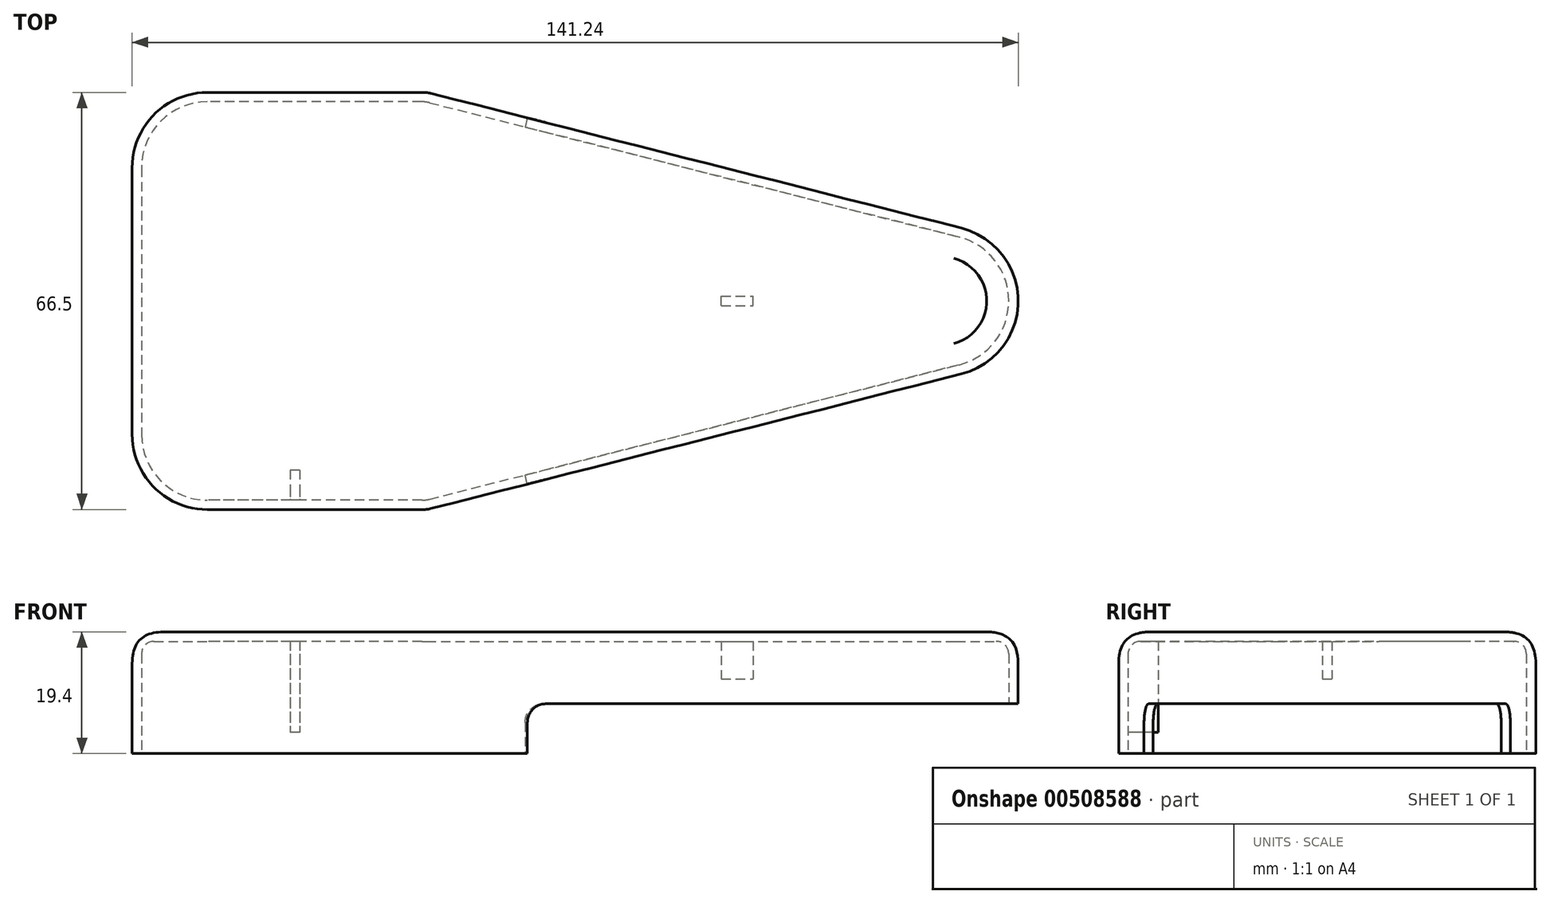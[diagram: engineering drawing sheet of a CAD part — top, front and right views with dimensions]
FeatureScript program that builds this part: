
annotation { "Feature Type Name" : "Feature", "Feature Type Description" : "" }
export const myFeature = defineFeature(function(context is Context, id is Id, definition is map)
    precondition{}
    {
        {
            var Q0;
            Q0=qCreatedBy(makeId("Top.planeOp"),FACE);
            var sketch = newSketch(context, id + "F0", { "sketchPlane" : qUnion([Q0])});
            skLineSegment(sketch, "E0.bottom", {"start": v(-70.61, 33.25) * mm, "end": v(70.61, 33.25) * mm, "construction": true});
            skLineSegment(sketch, "E0.top", {"start": v(-70.61, -33.25) * mm, "end": v(70.61, -33.25) * mm, "construction": true});
            skLineSegment(sketch, "E0.left", {"start": v(-70.61, 33.25) * mm, "end": v(-70.61, -33.25) * mm, "construction": true});
            skLineSegment(sketch, "E0.right", {"start": v(70.61, 33.25) * mm, "end": v(70.61, -33.25) * mm, "construction": true});
            skPoint(sketch, "E0.middle", {"position": v(0, 0) * mm});
            skLineSegment(sketch, "E1", {"start": v(-23.61, 33.25) * mm, "end": v(-23.62, -33.25) * mm, "construction": true});
            skArc(sketch, "E2", {"start": v(-58.62, 33.25) * mm, "mid": v(-67.1, 29.74) * mm, "end": v(-70.62, 21.25) * mm});
            skArc(sketch, "E3", {"start": v(-70.62, -21.25) * mm, "mid": v(-67.1, -29.74) * mm, "end": v(-58.62, -33.25) * mm});
            skArc(sketch, "E4", {"start": v(61.57, -11.63) * mm, "mid": v(70.61, 0) * mm, "end": v(61.57, 11.63) * mm});
            skLineSegment(sketch, "E5", {"start": v(-23.62, 33.25) * mm, "end": v(61.57, 11.63) * mm});
            skLineSegment(sketch, "E6", {"start": v(-23.62, -33.25) * mm, "end": v(61.57, -11.63) * mm});
            skLineSegment(sketch, "E7", {"start": v(-23.61, 33.25) * mm, "end": v(-58.62, 33.25) * mm});
            skLineSegment(sketch, "E8", {"start": v(-70.62, 21.25) * mm, "end": v(-70.62, -21.25) * mm});
            skLineSegment(sketch, "E9", {"start": v(-23.62, -33.25) * mm, "end": v(-58.62, -33.25) * mm});
            skSolve(sketch);
        }
        {
            var Q0;
            Q0=makeQuery(id+"F0.imprint","IMPRINT",FACE,{"disambiguationData":[TD([[makeQuery(id+"F0.imprint","IMPRINT",EDGE,{"derivedFrom":sQuery(id+"F0.wireOp",EDGE,"E2")}),1.0]])]});
            extrude(context, id + "F1", {"entities" : qUnion([Q0]), "depth" : 19.4 * mm, "offsetDistance" : 25 * mm});
        }
        {
            var Q0;
            Q0=makeQuery(id+"F1.opExtrude","CAP_FACE",FACE,{"disambiguationData":[OSD([sQuery(id+"F0.wireOp",EDGE,"E2"),sQuery(id+"F0.wireOp",EDGE,"E3"),sQuery(id+"F0.wireOp",EDGE,"E4"),sQuery(id+"F0.wireOp",EDGE,"E5"),sQuery(id+"F0.wireOp",EDGE,"E6"),sQuery(id+"F0.wireOp",EDGE,"E7"),sQuery(id+"F0.wireOp",EDGE,"E8"),sQuery(id+"F0.wireOp",EDGE,"E9")])],"isStart":true});
            shell(context, id + "F2", {"entities" : qUnion([Q0]), "thickness" : 1.5 * mm});
        }
        {
            var Q0;
            Q0=makeQuery(id+"F1.opExtrude","SWEPT_FACE",FACE,{"disambiguationData":[OSD([sQuery(id+"F0.wireOp",EDGE,"E9")])]});
            var sketch = newSketch(context, id + "F3", { "sketchPlane" : qUnion([Q0])});
            skLineSegment(sketch, "E10.0", {"start": v(-23.62, 19.4) * mm, "end": v(-58.62, 19.4) * mm, "construction": true});
            skLineSegment(sketch, "E11.0", {"start": v(-23.62, 0) * mm, "end": v(-58.62, 0) * mm, "construction": true});
            skLineSegment(sketch, "E12", {"start": v(-7.62, 7.94) * mm, "end": v(89.39, 7.94) * mm});
            skLineSegment(sketch, "E13", {"start": v(-7.62, 7.94) * mm, "end": v(-7.62, -17.76) * mm});
            skLineSegment(sketch, "E14", {"start": v(-7.62, -17.76) * mm, "end": v(89.39, -17.76) * mm});
            skLineSegment(sketch, "E15", {"start": v(89.39, -17.76) * mm, "end": v(89.39, 7.94) * mm});
            skSolve(sketch);
        }
        {
            var Q0;
            Q0=makeQuery(id+"F3.imprint","IMPRINT",FACE,{"disambiguationData":[TD([[makeQuery(id+"F3.imprint","IMPRINT",EDGE,{"derivedFrom":sQuery(id+"F3.wireOp",EDGE,"E12")}),-1.0]])]});
            extrude(context, id + "F4", {"entities" : qUnion([Q0]), "operationType" : NewBodyOperationType.REMOVE, "endBound" : BoundingType.THROUGH_ALL, "oppositeDirection" : true, "depth" : 117.7 * mm, "offsetDistance" : 25 * mm});
        }
        {
            var Q0;
            Q0=makeQuery(id+"F1.opExtrude","CAP_FACE",FACE,{"disambiguationData":[OSD([sQuery(id+"F0.wireOp",EDGE,"E2"),sQuery(id+"F0.wireOp",EDGE,"E3"),sQuery(id+"F0.wireOp",EDGE,"E4"),sQuery(id+"F0.wireOp",EDGE,"E5"),sQuery(id+"F0.wireOp",EDGE,"E6"),sQuery(id+"F0.wireOp",EDGE,"E7"),sQuery(id+"F0.wireOp",EDGE,"E8"),sQuery(id+"F0.wireOp",EDGE,"E9")])],"isStart":true});
            var sketch = newSketch(context, id + "F5", { "sketchPlane" : qUnion([Q0])});
            skLineSegment(sketch, "E16.0", {"start": v(61.2, 10.18) * mm, "end": v(-7.61, 27.64) * mm, "construction": true});
            skLineSegment(sketch, "E17.0", {"start": v(61.2, -10.18) * mm, "end": v(-7.62, -27.64) * mm, "construction": true});
            skLineSegment(sketch, "E18.0", {"start": v(61.57, 11.63) * mm, "end": v(-7.61, 29.19) * mm, "construction": true});
            skLineSegment(sketch, "E19.0", {"start": v(61.57, -11.63) * mm, "end": v(-7.61, -29.19) * mm, "construction": true});
            skLineSegment(sketch, "E20", {"start": v(-7.16, 31) * mm, "end": v(-8.52, 25.64) * mm});
            skLineSegment(sketch, "E21", {"start": v(-7.16, 31) * mm, "end": v(-6.28, 30.77) * mm});
            skLineSegment(sketch, "E22", {"start": v(-6.28, 30.77) * mm, "end": v(-7.64, 25.41) * mm});
            skLineSegment(sketch, "E23", {"start": v(-8.52, 25.64) * mm, "end": v(-7.64, 25.41) * mm});
            skLineSegment(sketch, "E24.MirrorCS", {"start": v(-6.28, -30.77) * mm, "end": v(-7.64, -25.41) * mm});
            skLineSegment(sketch, "E25.MirrorCS", {"start": v(-7.16, -31) * mm, "end": v(-6.28, -30.77) * mm});
            skLineSegment(sketch, "E26.MirrorCS", {"start": v(-7.16, -31) * mm, "end": v(-8.52, -25.64) * mm});
            skLineSegment(sketch, "E27.MirrorCS", {"start": v(-8.52, -25.64) * mm, "end": v(-7.64, -25.41) * mm});
            skSolve(sketch);
        }
        {
            var Q0;
            {var subQ1=sQuery(id+"F0.wireOp",EDGE,"E5");var subQ2=makeQuery(id+"F4.boolean.opBoolean","INTERSECT",EDGE,{"disambiguationData":[OD(0.0)],"derivedFrom":[makeQuery(id+"F1.opExtrude","CAP_FACE",FACE,{"disambiguationData":[OSD([sQuery(id+"F0.wireOp",EDGE,"E2"),sQuery(id+"F0.wireOp",EDGE,"E3"),sQuery(id+"F0.wireOp",EDGE,"E4"),subQ1,sQuery(id+"F0.wireOp",EDGE,"E6"),sQuery(id+"F0.wireOp",EDGE,"E7"),sQuery(id+"F0.wireOp",EDGE,"E8"),sQuery(id+"F0.wireOp",EDGE,"E9")])],"isStart":true}),makeQuery(id+"F4.opExtrude","SWEPT_FACE",FACE,{"disambiguationData":[OSD([sQuery(id+"F3.wireOp",EDGE,"E13")])]})]});Q0=makeQuery(id+"F5.imprint","IMPRINT",FACE,{"disambiguationData":[TD([[makeQuery(id+"F5.imprint","IMPRINT",EDGE,{"derivedFrom":subQ2}),1.0]])]});}
            var Q1;
            {var subQ1=sQuery(id+"F0.wireOp",EDGE,"E6");var subQ2=makeQuery(id+"F4.boolean.opBoolean","INTERSECT",EDGE,{"disambiguationData":[OD(1.0)],"derivedFrom":[makeQuery(id+"F1.opExtrude","CAP_FACE",FACE,{"disambiguationData":[OSD([sQuery(id+"F0.wireOp",EDGE,"E2"),sQuery(id+"F0.wireOp",EDGE,"E3"),sQuery(id+"F0.wireOp",EDGE,"E4"),sQuery(id+"F0.wireOp",EDGE,"E5"),subQ1,sQuery(id+"F0.wireOp",EDGE,"E7"),sQuery(id+"F0.wireOp",EDGE,"E8"),sQuery(id+"F0.wireOp",EDGE,"E9")])],"isStart":true}),makeQuery(id+"F4.opExtrude","SWEPT_FACE",FACE,{"disambiguationData":[OSD([sQuery(id+"F3.wireOp",EDGE,"E13")])]})]});Q1=makeQuery(id+"F5.imprint","IMPRINT",FACE,{"disambiguationData":[TD([[makeQuery(id+"F5.imprint","IMPRINT",EDGE,{"derivedFrom":subQ2}),1.0]])]});}
            var Q2;
            Q2=makeQuery(id+"F4.boolean.opBoolean","COPY",FACE,{"derivedFrom":makeQuery(id+"F4.opExtrude","SWEPT_FACE",FACE,{"disambiguationData":[OSD([sQuery(id+"F3.wireOp",EDGE,"E12")])]})});
            extrude(context, id + "F6", {"entities" : qUnion([Q0, Q1]), "operationType" : NewBodyOperationType.REMOVE, "endBound" : BoundingType.UP_TO_SURFACE, "oppositeDirection" : true, "depth" : 25 * mm, "endBoundEntityFace" : qUnion([Q2]), "offsetDistance" : 25 * mm});
        }
        {
            var Q0;
            Q0=makeQuery(id+"F2.opShell","OFFSET_FACE",FACE,{"disambiguationData":[OSD([sQuery(id+"F0.wireOp",EDGE,"E2"),sQuery(id+"F0.wireOp",EDGE,"E3"),sQuery(id+"F0.wireOp",EDGE,"E4"),sQuery(id+"F0.wireOp",EDGE,"E5"),sQuery(id+"F0.wireOp",EDGE,"E6"),sQuery(id+"F0.wireOp",EDGE,"E7"),sQuery(id+"F0.wireOp",EDGE,"E8"),sQuery(id+"F0.wireOp",EDGE,"E9")])]});
            cPlane(context, id + "F7", {"entities" : qUnion([Q0]), "cplaneType" : CPlaneType.OFFSET, "offset" : 14.5 * mm, "width" : 150 * mm, "height" : 150 * mm});
        }
        {
            var Q0;
            Q0=qCreatedBy(id+"F7.planeOp",FACE);
            var sketch = newSketch(context, id + "F8", { "sketchPlane" : qUnion([Q0])});
            skLineSegment(sketch, "E28.0", {"start": v(-70.62, -21.25) * mm, "end": v(-70.62, 21.25) * mm, "construction": true});
            skLineSegment(sketch, "E29.0", {"start": v(-23.8, -31.75) * mm, "end": v(-58.62, -31.75) * mm, "construction": true});
            skLineSegment(sketch, "E30", {"start": v(-43.92, 31.75) * mm, "end": v(-43.91, -31.75) * mm, "construction": true});
            skLineSegment(sketch, "E31", {"start": v(-57.03, 26.95) * mm, "end": v(-36.15, 26.95) * mm, "construction": true});
            skLineSegment(sketch, "E32.0", {"start": v(-23.62, 33.25) * mm, "end": v(-58.62, 33.25) * mm, "construction": true});
            skPoint(sketch, "E33.orphan", {"position": v(-58.62, 31.75) * mm});
            skPoint(sketch, "E34.0.start.orphan", {"position": v(-23.8, 31.75) * mm});
            skLineSegment(sketch, "E35.0", {"start": v(-23.8, 31.75) * mm, "end": v(-58.62, 31.75) * mm, "construction": true});
            skPoint(sketch, "E36", {"position": v(-43.92, 26.95) * mm});
            skLineSegment(sketch, "E37.bottom", {"start": v(-43.92, 26.95) * mm, "end": v(-45.42, 26.95) * mm});
            skLineSegment(sketch, "E37.top", {"start": v(-43.92, 31.75) * mm, "end": v(-45.42, 31.75) * mm});
            skLineSegment(sketch, "E37.left", {"start": v(-43.92, 26.95) * mm, "end": v(-43.92, 31.75) * mm});
            skLineSegment(sketch, "E37.right", {"start": v(-45.42, 26.95) * mm, "end": v(-45.42, 31.75) * mm});
            skSolve(sketch);
        }
        {
            var Q0;
            {var subQ0=sQuery(id+"F0.wireOp",EDGE,"E9");Q0=makeQuery(id+"F2.opShell","OFFSET_EDGE",EDGE,{"disambiguationData":[OSD([subQ0]),TDD([makeQuery(id+"F1.opExtrude","CAP_EDGE",EDGE,{"disambiguationData":[OSD([subQ0])],"isStart":false})])]});}
            var Q1;
            {var subQ0=sQuery(id+"F0.wireOp",EDGE,"E6");Q1=makeQuery(id+"F2.opShell","OFFSET_EDGE",EDGE,{"disambiguationData":[OSD([subQ0]),TDD([makeQuery(id+"F1.opExtrude","CAP_EDGE",EDGE,{"disambiguationData":[OSD([subQ0])],"isStart":false})])]});}
            fillet(context, id + "F9", {"entities" : qUnion([Q0, Q1]), "radius" : 2 * mm, "tangentPropagation" : true, "allowEdgeOverflow" : false});
        }
        {
            var Q0;
            Q0=makeQuery(id+"F8.imprint","IMPRINT",FACE,{"disambiguationData":[TD([[makeQuery(id+"F8.imprint","IMPRINT",EDGE,{"derivedFrom":sQuery(id+"F8.wireOp",EDGE,"E37.bottom")}),-1.0]])]});
            extrude(context, id + "F10", {"entities" : qUnion([Q0]), "operationType" : NewBodyOperationType.ADD, "endBound" : BoundingType.UP_TO_NEXT, "oppositeDirection" : true, "depth" : 25 * mm, "offsetDistance" : 25 * mm});
        }
        {
            var Q0;
            Q0=makeQuery(id+"F2.opShell","OFFSET_FACE",FACE,{"disambiguationData":[OSD([sQuery(id+"F0.wireOp",EDGE,"E2"),sQuery(id+"F0.wireOp",EDGE,"E3"),sQuery(id+"F0.wireOp",EDGE,"E4"),sQuery(id+"F0.wireOp",EDGE,"E5"),sQuery(id+"F0.wireOp",EDGE,"E6"),sQuery(id+"F0.wireOp",EDGE,"E7"),sQuery(id+"F0.wireOp",EDGE,"E8"),sQuery(id+"F0.wireOp",EDGE,"E9")])]});
            var sketch = newSketch(context, id + "F11", { "sketchPlane" : qUnion([Q0])});
            skLineSegment(sketch, "E38.0", {"start": v(-70.62, -21.25) * mm, "end": v(-70.62, 21.25) * mm, "construction": true});
            skLineSegment(sketch, "E39", {"start": v(-24.76, 0) * mm, "end": v(55.29, 0) * mm, "construction": true});
            skLineSegment(sketch, "E40", {"start": v(28.38, 14.2) * mm, "end": v(28.38, -12.8) * mm, "construction": true});
            skLineSegment(sketch, "E41", {"start": v(23.28, 11.59) * mm, "end": v(23.28, -11.77) * mm, "construction": true});
            skLineSegment(sketch, "E42.bottom", {"start": v(23.28, 0.75) * mm, "end": v(28.38, 0.75) * mm});
            skLineSegment(sketch, "E42.top", {"start": v(23.28, -0.75) * mm, "end": v(28.38, -0.75) * mm});
            skLineSegment(sketch, "E42.left", {"start": v(23.28, 0.75) * mm, "end": v(23.28, -0.75) * mm});
            skLineSegment(sketch, "E42.right", {"start": v(28.38, 0.75) * mm, "end": v(28.38, -0.75) * mm});
            skPoint(sketch, "E42.middle", {"position": v(25.83, 0) * mm});
            skSolve(sketch);
        }
        {
            var Q0;
            Q0=makeQuery(id+"F11.imprint","IMPRINT",FACE,{"disambiguationData":[TD([[makeQuery(id+"F11.imprint","IMPRINT",EDGE,{"derivedFrom":sQuery(id+"F11.wireOp",EDGE,"E42.bottom")}),1.0]])]});
            cPlane(context, id + "F12", {"entities" : qUnion([Q0]), "cplaneType" : CPlaneType.OFFSET, "offset" : 6 * mm, "width" : 150 * mm, "height" : 150 * mm});
        }
        {
            var Q0;
            Q0=qCreatedBy(id+"F12.planeOp",FACE);
            var sketch = newSketch(context, id + "F13", { "sketchPlane" : qUnion([Q0])});
            skLineSegment(sketch, "E43.0", {"start": v(23.28, -0.75) * mm, "end": v(28.38, -0.75) * mm});
            skLineSegment(sketch, "E44.0", {"start": v(23.28, 0.75) * mm, "end": v(28.38, 0.75) * mm});
            skLineSegment(sketch, "E45.0", {"start": v(28.38, 0.75) * mm, "end": v(28.38, -0.75) * mm});
            skLineSegment(sketch, "E46.0", {"start": v(23.28, 0.75) * mm, "end": v(23.28, -0.75) * mm});
            skSolve(sketch);
        }
        {
            var Q0;
            Q0=makeQuery(id+"F13.imprint","IMPRINT",FACE,{"disambiguationData":[TD([[makeQuery(id+"F13.imprint","IMPRINT",EDGE,{"derivedFrom":sQuery(id+"F13.wireOp",EDGE,"E43.0")}),1.0]])]});
            extrude(context, id + "F14", {"entities" : qUnion([Q0]), "operationType" : NewBodyOperationType.ADD, "endBound" : BoundingType.UP_TO_NEXT, "oppositeDirection" : true, "depth" : 25 * mm, "offsetDistance" : 25 * mm});
        }
        {
            var Q0;
            Q0=makeQuery(id+"F1.opExtrude","SWEPT_EDGE",EDGE,{"disambiguationData":[OSD([sQuery(id+"F0.wireOp",EDGE,"E6"),sQuery(id+"F0.wireOp",EDGE,"E9")])]});
            var Q1;
            Q1=makeQuery(id+"F1.opExtrude","SWEPT_EDGE",EDGE,{"disambiguationData":[OSD([sQuery(id+"F0.wireOp",EDGE,"E5"),sQuery(id+"F0.wireOp",EDGE,"E7")])]});
            fillet(context, id + "F15", {"entities" : qUnion([Q0, Q1]), "radius" : 5 * mm, "tangentPropagation" : true, "rho" : 0.5, "crossSection" : FilletCrossSection.CONIC, "allowEdgeOverflow" : false});
        }
        {
            var Q0;
            Q0=makeQuery(id+"F1.opExtrude","CAP_FACE",FACE,{"disambiguationData":[OSD([sQuery(id+"F0.wireOp",EDGE,"E2"),sQuery(id+"F0.wireOp",EDGE,"E3"),sQuery(id+"F0.wireOp",EDGE,"E4"),sQuery(id+"F0.wireOp",EDGE,"E5"),sQuery(id+"F0.wireOp",EDGE,"E6"),sQuery(id+"F0.wireOp",EDGE,"E7"),sQuery(id+"F0.wireOp",EDGE,"E8"),sQuery(id+"F0.wireOp",EDGE,"E9")])],"isStart":false});
            fillet(context, id + "F16", {"entities" : qUnion([Q0]), "radius" : 5 * mm, "tangentPropagation" : true, "rho" : 0.5, "crossSection" : FilletCrossSection.CONIC, "allowEdgeOverflow" : false});
        }
        {
            var Q0;
            Q0=makeQuery(id+"F6.boolean.opBoolean","COPY",EDGE,{"derivedFrom":makeQuery(id+"F6.opExtrude","CAP_EDGE",EDGE,{"disambiguationData":[OSD([sQuery(id+"F5.wireOp",EDGE,"E20")])],"isStart":true})});
            var Q1;
            Q1=makeQuery(id+"F6.boolean.opBoolean","COPY",EDGE,{"derivedFrom":makeQuery(id+"F6.opExtrude","CAP_EDGE",EDGE,{"disambiguationData":[OSD([sQuery(id+"F5.wireOp",EDGE,"E20")])],"isStart":false})});
            var Q2;
            Q2=makeQuery(id+"F6.boolean.opBoolean","COPY",EDGE,{"derivedFrom":makeQuery(id+"F6.opExtrude","CAP_EDGE",EDGE,{"disambiguationData":[OSD([sQuery(id+"F5.wireOp",EDGE,"E26.MirrorCS")])],"isStart":true})});
            var Q3;
            Q3=makeQuery(id+"F6.boolean.opBoolean","COPY",EDGE,{"derivedFrom":makeQuery(id+"F6.opExtrude","CAP_EDGE",EDGE,{"disambiguationData":[OSD([sQuery(id+"F5.wireOp",EDGE,"E26.MirrorCS")])],"isStart":false})});
            fillet(context, id + "F17", {"entities" : qUnion([Q0, Q1, Q2, Q3]), "radius" : 3 * mm, "tangentPropagation" : true, "allowEdgeOverflow" : false});
        }
        {
            var Q0;
            Q0=qCreatedBy(makeId("Front.planeOp"),FACE);
            var sketch = newSketch(context, id + "F18", { "sketchPlane" : qUnion([Q0])});
            skLineSegment(sketch, "E47", {"start": v(0, 0) * mm, "end": v(0, 44.21) * mm, "construction": true});
            skSolve(sketch);
        }
        {
            var Q0;
            Q0=makeQuery(id+"F2.opShell","OFFSET_EDGE",EDGE,{"disambiguationData":[OSD([sQuery(id+"F0.wireOp",EDGE,"E6"),sQuery(id+"F0.wireOp",EDGE,"E9")])]});
            var Q1;
            Q1=makeQuery(id+"F2.opShell","OFFSET_EDGE",EDGE,{"disambiguationData":[OSD([sQuery(id+"F0.wireOp",EDGE,"E5"),sQuery(id+"F0.wireOp",EDGE,"E7")])]});
            fillet(context, id + "F19", {"entities" : qUnion([Q0, Q1]), "radius" : 5 * mm, "tangentPropagation" : true, "allowEdgeOverflow" : false});
        }
    });
